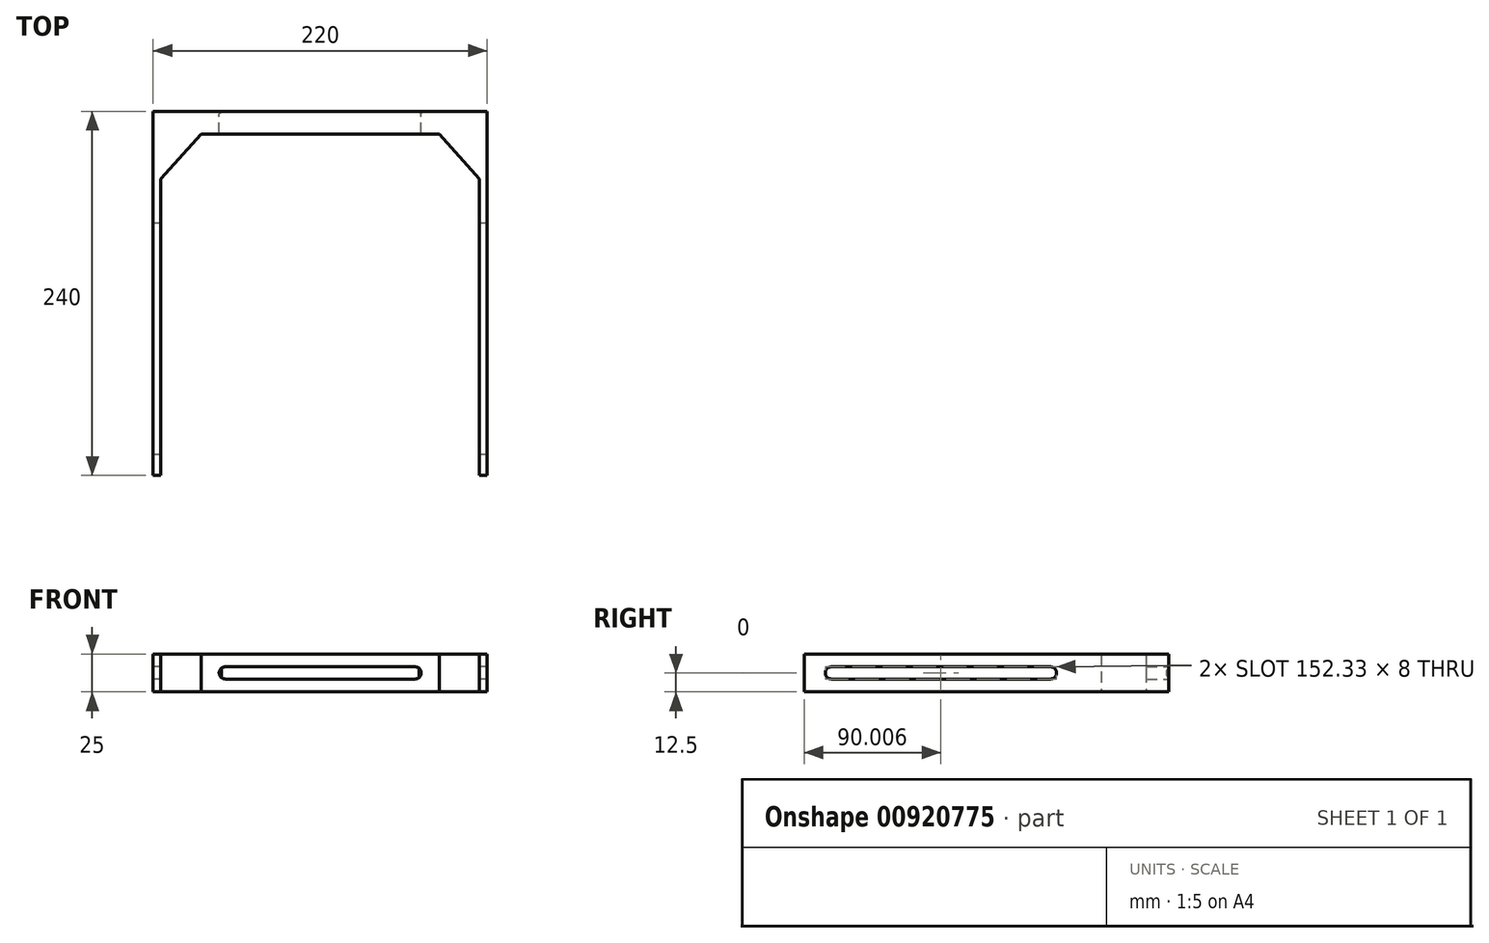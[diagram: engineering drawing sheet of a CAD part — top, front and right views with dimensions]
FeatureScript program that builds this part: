
annotation { "Feature Type Name" : "Feature", "Feature Type Description" : "" }
export const myFeature = defineFeature(function(context is Context, id is Id, definition is map)
    precondition{}
    {
        {
            var Q0;
            Q0=qCreatedBy(makeId("Front.planeOp"),FACE);
            var sketch = newSketch(context, id + "F0", { "sketchPlane" : qUnion([Q0])});
            skLineSegment(sketch, "E0.bottom", {"start": v(110, 12.5) * mm, "end": v(-110, 12.5) * mm});
            skLineSegment(sketch, "E0.top", {"start": v(110, -12.5) * mm, "end": v(-110, -12.5) * mm});
            skLineSegment(sketch, "E0.left", {"start": v(110, 12.5) * mm, "end": v(110, -12.5) * mm});
            skLineSegment(sketch, "E0.right", {"start": v(-110, 12.5) * mm, "end": v(-110, -12.5) * mm});
            skPoint(sketch, "E0.middle", {"position": v(0, 0) * mm});
            skLineSegment(sketch, "E1.bottom", {"start": v(62.5, 4) * mm, "end": v(-62.5, 4) * mm});
            skLineSegment(sketch, "E1.top", {"start": v(62.5, -4) * mm, "end": v(-62.5, -4) * mm});
            skLineSegment(sketch, "E1.left", {"start": v(62.5, 4) * mm, "end": v(62.5, -4) * mm});
            skLineSegment(sketch, "E1.right", {"start": v(-62.5, 4) * mm, "end": v(-62.5, -4) * mm});
            skArc(sketch, "E2", {"start": v(-62.5, 4) * mm, "mid": v(-66.5, 0) * mm, "end": v(-62.5, -4) * mm});
            skArc(sketch, "E3", {"start": v(62.5, -4) * mm, "mid": v(66.5, 0) * mm, "end": v(62.5, 4) * mm});
            skSolve(sketch);
        }
        {
            var Q0;
            Q0 = qSketchRegion(id + "F0", true);
            extrude(context, id + "F1", {"entities" : qUnion([Q0]), "depth" : 15 * mm, "offsetDistance" : 25 * mm});
        }
        {
            var Q0;
            Q0=makeQuery(id+"F1.opExtrude","CAP_FACE",FACE,{"disambiguationData":[OSD([sQuery(id+"F0.wireOp",EDGE,"E0.bottom"),sQuery(id+"F0.wireOp",EDGE,"E0.top"),sQuery(id+"F0.wireOp",EDGE,"E0.left"),sQuery(id+"F0.wireOp",EDGE,"E0.right"),sQuery(id+"F0.wireOp",EDGE,"E1.bottom"),sQuery(id+"F0.wireOp",EDGE,"E1.top"),sQuery(id+"F0.wireOp",EDGE,"E2"),sQuery(id+"F0.wireOp",EDGE,"E3")])],"isStart":false});
            var sketch = newSketch(context, id + "F2", { "sketchPlane" : qUnion([Q0])});
            skLineSegment(sketch, "E4.bottom", {"start": v(-110, 12.5) * mm, "end": v(-105, 12.5) * mm});
            skLineSegment(sketch, "E4.top", {"start": v(-110, -12.5) * mm, "end": v(-105, -12.5) * mm});
            skLineSegment(sketch, "E4.left", {"start": v(-110, 12.5) * mm, "end": v(-110, -12.5) * mm});
            skLineSegment(sketch, "E4.right", {"start": v(-105, 12.5) * mm, "end": v(-105, -12.5) * mm});
            skLineSegment(sketch, "E5.bottom", {"start": v(110, 12.5) * mm, "end": v(105, 12.5) * mm});
            skLineSegment(sketch, "E5.top", {"start": v(110, -12.5) * mm, "end": v(105, -12.5) * mm});
            skLineSegment(sketch, "E5.left", {"start": v(110, 12.5) * mm, "end": v(110, -12.5) * mm});
            skLineSegment(sketch, "E5.right", {"start": v(105, 12.5) * mm, "end": v(105, -12.5) * mm});
            skSolve(sketch);
        }
        {
            var Q0;
            Q0 = qSketchRegion(id + "F2", true);
            extrude(context, id + "F3", {"entities" : qUnion([Q0]), "operationType" : NewBodyOperationType.ADD, "depth" : 225 * mm, "offsetDistance" : 25 * mm});
        }
        {
            var Q0;
            Q0=makeQuery(id+"F3.boolean.opBoolean","MERGE",FACE,{"derivedFrom":[makeQuery(id+"F1.opExtrude","SWEPT_FACE",FACE,{"disambiguationData":[OSD([sQuery(id+"F0.wireOp",EDGE,"E0.top")])]}),makeQuery(id+"F3.opExtrude","SWEPT_FACE",FACE,{"disambiguationData":[OSD([sQuery(id+"F2.wireOp",EDGE,"E4.top")])]}),makeQuery(id+"F3.opExtrude","SWEPT_FACE",FACE,{"disambiguationData":[OSD([sQuery(id+"F2.wireOp",EDGE,"E5.top")])]})]});
            var sketch = newSketch(context, id + "F4", { "sketchPlane" : qUnion([Q0])});
            skLineSegment(sketch, "E6", {"start": v(-65, 0) * mm, "end": v(-110, 50) * mm});
            skLineSegment(sketch, "E7", {"start": v(-110, 50) * mm, "end": v(-110, 0) * mm});
            skLineSegment(sketch, "E8", {"start": v(-110, 0) * mm, "end": v(-65, 0) * mm});
            skLineSegment(sketch, "E9", {"start": v(110, 0) * mm, "end": v(110, 50) * mm});
            skLineSegment(sketch, "E10", {"start": v(110, 50) * mm, "end": v(65, 0) * mm});
            skLineSegment(sketch, "E11", {"start": v(65, 0) * mm, "end": v(110, 0) * mm});
            skSolve(sketch);
        }
        {
            var Q0;
            Q0 = qSketchRegion(id + "F4", true);
            extrude(context, id + "F5", {"entities" : qUnion([Q0]), "operationType" : NewBodyOperationType.ADD, "oppositeDirection" : true, "depth" : 25 * mm, "offsetDistance" : 25 * mm});
        }
        {
            var Q0;
            Q0=makeQuery(id+"F3.boolean.opBoolean","MERGE",FACE,{"derivedFrom":[makeQuery(id+"F1.opExtrude","SWEPT_FACE",FACE,{"disambiguationData":[OSD([sQuery(id+"F0.wireOp",EDGE,"E0.right")])]}),makeQuery(id+"F3.opExtrude","SWEPT_FACE",FACE,{"disambiguationData":[OSD([sQuery(id+"F2.wireOp",EDGE,"E4.left")])]})]});
            var sketch = newSketch(context, id + "F6", { "sketchPlane" : qUnion([Q0])});
            skLineSegment(sketch, "E12", {"start": v(150, 12.5) * mm, "end": v(150, -12.5) * mm});
            skLineSegment(sketch, "E13.bottom", {"start": v(222.16, 4) * mm, "end": v(77.83, 4) * mm});
            skLineSegment(sketch, "E13.top", {"start": v(222.16, -4) * mm, "end": v(77.83, -4) * mm});
            skLineSegment(sketch, "E13.left", {"start": v(222.16, 4) * mm, "end": v(222.16, -4) * mm});
            skLineSegment(sketch, "E13.right", {"start": v(77.83, 4) * mm, "end": v(77.83, -4) * mm});
            skPoint(sketch, "E13.middle", {"position": v(150, 0) * mm});
            skArc(sketch, "E14", {"start": v(77.83, 4) * mm, "mid": v(73.83, 0) * mm, "end": v(77.83, -4) * mm});
            skArc(sketch, "E15", {"start": v(222.16, -4) * mm, "mid": v(226.16, 0) * mm, "end": v(222.16, 4) * mm});
            skSolve(sketch);
        }
        {
            var Q0;
            Q0 = qSketchRegion(id + "F6", true);
            extrude(context, id + "F7", {"entities" : qUnion([Q0]), "operationType" : NewBodyOperationType.REMOVE, "oppositeDirection" : true, "depth" : 256 * mm, "offsetDistance" : 25 * mm});
        }
    });
